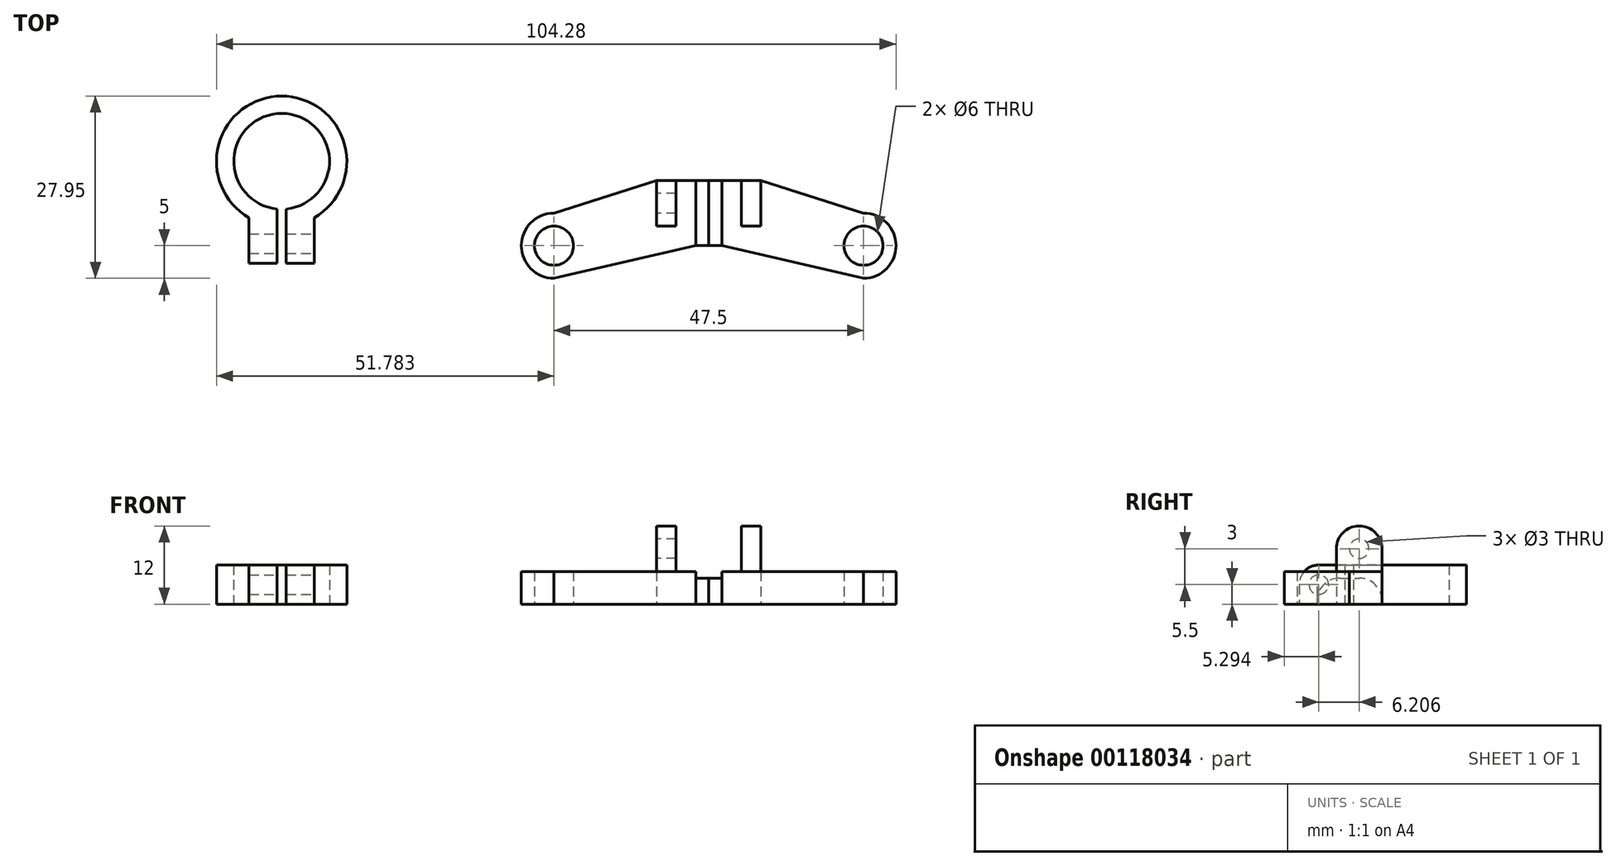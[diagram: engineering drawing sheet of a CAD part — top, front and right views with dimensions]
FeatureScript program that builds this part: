
annotation { "Feature Type Name" : "Feature", "Feature Type Description" : "" }
export const myFeature = defineFeature(function(context is Context, id is Id, definition is map)
    precondition{}
    {
        {
            var Q0;
            Q0=qCreatedBy(makeId("Top.planeOp"),FACE);
            var sketch = newSketch(context, id + "F0", { "sketchPlane" : qUnion([Q0])});
            skCircle(sketch, "E0", {"center": v(-31.45, 17.95) * mm, "radius": 7.35 * mm});
            skCircle(sketch, "E1", {"center": v(-31.45, 17.95) * mm, "radius": 10 * mm});
            skLineSegment(sketch, "E2", {"start": v(-26.45, 9.3) * mm, "end": v(-26.45, 2.3) * mm});
            skLineSegment(sketch, "E3", {"start": v(-26.45, 2.3) * mm, "end": v(-36.45, 2.3) * mm});
            skLineSegment(sketch, "E4", {"start": v(-36.45, 2.3) * mm, "end": v(-36.45, 9.3) * mm});
            skLineSegment(sketch, "E5", {"start": v(-32.15, 2.3) * mm, "end": v(-32.15, 10.64) * mm});
            skLineSegment(sketch, "E6", {"start": v(-30.75, 2.3) * mm, "end": v(-30.75, 10.64) * mm});
            skSolve(sketch);
        }
        {
            var Q0;
            {var subQ0=sQuery(id+"F0.wireOp",EDGE,"E2");Q0=makeQuery(id+"F0.imprint","IMPRINT",FACE,{"disambiguationData":[TD([[makeQuery(id+"F0.imprint","IMPRINT",EDGE,{"derivedFrom":subQ0}),-1.0]])]});}
            var Q1;
            {var subQ0=sQuery(id+"F0.wireOp",EDGE,"E4");Q1=makeQuery(id+"F0.imprint","IMPRINT",FACE,{"disambiguationData":[TD([[makeQuery(id+"F0.imprint","IMPRINT",EDGE,{"derivedFrom":subQ0}),-1.0]])]});}
            var Q2;
            {var subQ3=sQuery(id+"F0.wireOp",EDGE,"E5");var subQ4=sQuery(id+"F0.wireOp",EDGE,"E0");var subQ5=makeQuery(id+"F0.imprint","INTERSECT",VERTEX,{"derivedFrom":[subQ4,subQ3]});Q2=makeQuery(id+"F0.imprint","IMPRINT",FACE,{"disambiguationData":[TD([[makeQuery(id+"F0.imprint","IMPRINT",EDGE,{"disambiguationData":[TD([[subQ5,1.0]])],"derivedFrom":subQ4}),-1.0]])]});}
            extrude(context, id + "F1", {"entities" : qUnion([Q0, Q1, Q2]), "depth" : 6 * mm});
        }
        {
            var Q0;
            Q0=makeQuery(id+"F1.opExtrude","SWEPT_FACE",FACE,{"disambiguationData":[OSD([sQuery(id+"F0.wireOp",EDGE,"E2")])]});
            var sketch = newSketch(context, id + "F2", { "sketchPlane" : qUnion([Q0])});
            skPoint(sketch, "E7", {"position": v(5.3, 3) * mm});
            skSolve(sketch);
        }
        {
            var Q0;
            Q0=sQuery(id+"F2.wireOp",VERTEX,"E7");
            var Q1;
            Q1=makeQuery(id+"F1.opExtrude","SWEPT_BODY",BODY,{"disambiguationData":[OSD([sQuery(id+"F0.wireOp",EDGE,"E0"),sQuery(id+"F0.wireOp",EDGE,"E1"),sQuery(id+"F0.wireOp",EDGE,"E2"),sQuery(id+"F0.wireOp",EDGE,"E3"),sQuery(id+"F0.wireOp",EDGE,"E4")])]});
            hole(context, id + "F3", {"style" : HoleStyle.SIMPLE, "endStyle" : HoleEndStyle.THROUGH, "holeDiameter" : 3 * mm, "locations" : qUnion([Q0]), "scope" : qUnion([Q1]), "isTappedThrough" : true});
        }
        {
            var Q0;
            Q0=qCreatedBy(makeId("Top.planeOp"),FACE);
            var sketch = newSketch(context, id + "F4", { "sketchPlane" : qUnion([Q0])});
            skCircle(sketch, "E8", {"center": v(10.33, 5) * mm, "radius": 3 * mm});
            skLineSegment(sketch, "E9.left", {"start": v(5.33, 10) * mm, "end": v(5.33, 0) * mm});
            skPoint(sketch, "E10", {"position": v(10.33, 0) * mm});
            skPoint(sketch, "E11", {"position": v(34.08, 5) * mm});
            skLineSegment(sketch, "E12", {"start": v(34.08, 5) * mm, "end": v(32.08, 5) * mm});
            skLineSegment(sketch, "E13", {"start": v(32.08, 5) * mm, "end": v(10.33, 0) * mm});
            skPoint(sketch, "E14", {"position": v(29.08, 8) * mm});
            skPoint(sketch, "E15", {"position": v(26.08, 8) * mm});
            skLineSegment(sketch, "E16", {"start": v(26.08, 8) * mm, "end": v(26.08, 15) * mm});
            skLineSegment(sketch, "E17", {"start": v(34.08, 15) * mm, "end": v(26.08, 15) * mm});
            skLineSegment(sketch, "E18", {"start": v(29.08, 8) * mm, "end": v(29.08, 15) * mm});
            skPoint(sketch, "E19", {"position": v(32.08, 15) * mm});
            skLineSegment(sketch, "E20", {"start": v(32.08, 5) * mm, "end": v(32.08, 8) * mm});
            skPoint(sketch, "E21", {"position": v(10.33, 10) * mm});
            skPoint(sketch, "E22", {"position": v(26.08, 11.5) * mm});
            skLineSegment(sketch, "E23", {"start": v(32.08, 15) * mm, "end": v(32.08, 8) * mm});
            skLineSegment(sketch, "E24", {"start": v(5.33, 10) * mm, "end": v(10.33, 10) * mm});
            skLineSegment(sketch, "E25", {"start": v(5.33, 0) * mm, "end": v(10.33, 0) * mm});
            skLineSegment(sketch, "E26", {"start": v(26.08, 8) * mm, "end": v(29.08, 8) * mm});
            skLineSegment(sketch, "E27", {"start": v(29.08, 8) * mm, "end": v(32.08, 8) * mm});
            skLineSegment(sketch, "E28", {"start": v(34.08, 5) * mm, "end": v(34.08, 15) * mm});
            skLineSegment(sketch, "E29", {"start": v(10.33, 10) * mm, "end": v(26.08, 15) * mm});
            skSolve(sketch);
        }
        {
            var Q0;
            {var subQ0=sQuery(id+"F4.wireOp",EDGE,"E16");Q0=makeQuery(id+"F4.imprint","IMPRINT",FACE,{"disambiguationData":[TD([[makeQuery(id+"F4.imprint","IMPRINT",EDGE,{"derivedFrom":subQ0}),-1.0]])]});}
            extrude(context, id + "F5", {"entities" : qUnion([Q0]), "depth" : 12 * mm});
        }
        {
            var Q0;
            Q0=makeQuery(id+"F4.imprint","IMPRINT",FACE,{"disambiguationData":[TD([[makeQuery(id+"F4.imprint","IMPRINT",EDGE,{"derivedFrom":sQuery(id+"F4.wireOp",EDGE,"E8")}),-1.0]])]});
            var Q1;
            {var subQ0=sQuery(id+"F4.wireOp",EDGE,"E18");Q1=makeQuery(id+"F4.imprint","IMPRINT",FACE,{"disambiguationData":[TD([[makeQuery(id+"F4.imprint","IMPRINT",EDGE,{"derivedFrom":subQ0}),-1.0]])]});}
            var Q2;
            {var subQ3=sQuery(id+"F4.wireOp",EDGE,"1xFQyo0G-Xs1s-Fqlw-DN10-UjsStAcqlzeH");Q2=makeQuery(id+"F4.imprint","IMPRINT",FACE,{"disambiguationData":[TD([[makeQuery(id+"F4.imprint","IMPRINT",EDGE,{"derivedFrom":subQ3}),1.0]])]});}
            extrude(context, id + "F6", {"entities" : qUnion([Q0, Q1, Q2]), "operationType" : NewBodyOperationType.ADD, "depth" : 5 * mm});
        }
        {
            var Q0;
            {var subQ3=sQuery(id+"F4.wireOp",EDGE,"uUS1zDU1-sOwB-zFEP-Xbho-WG0gHNYcOc71");Q0=makeQuery(id+"F4.imprint","IMPRINT",FACE,{"disambiguationData":[TD([[makeQuery(id+"F4.imprint","IMPRINT",EDGE,{"derivedFrom":subQ3}),-1.0]])]});}
            var Q1;
            {var subQ4=sQuery(id+"F4.wireOp",EDGE,"E12");Q1=makeQuery(id+"F4.imprint","IMPRINT",FACE,{"disambiguationData":[TD([[makeQuery(id+"F4.imprint","IMPRINT",EDGE,{"derivedFrom":subQ4}),-1.0]])]});}
            var Q2;
            {var subQ1=sQuery(id+"F4.wireOp",EDGE,"N1TZ5UtL-Frhi-5IxH-qIdc-fXHmOs3rLAIg");Q2=makeQuery(id+"F4.imprint","IMPRINT",FACE,{"disambiguationData":[TD([[makeQuery(id+"F4.imprint","IMPRINT",EDGE,{"derivedFrom":subQ1}),1.0]])]});}
            extrude(context, id + "F7", {"entities" : qUnion([Q0, Q1, Q2]), "operationType" : NewBodyOperationType.ADD, "depth" : 4 * mm});
        }
        {
            var Q0;
            Q0=makeQuery(id+"F6.opExtrude","SWEPT_EDGE",EDGE,{"disambiguationData":[OSD([sQuery(id+"F4.wireOp",EDGE,"E9.top"),sQuery(id+"F4.wireOp",EDGE,"E9.left")])]});
            var Q1;
            Q1=makeQuery(id+"F6.opExtrude","SWEPT_EDGE",EDGE,{"disambiguationData":[OSD([sQuery(id+"F4.wireOp",EDGE,"E9.bottom"),sQuery(id+"F4.wireOp",EDGE,"E9.left")])]});
            fillet(context, id + "F8", {"entities" : qUnion([Q0, Q1]), "radius" : 5 * mm, "tangentPropagation" : true, "allowEdgeOverflow" : false});
        }
        {
            var Q0;
            {var subQ0=makeQuery(id+"F7.opExtrude","CAP_EDGE",EDGE,{"disambiguationData":[OSD([sQuery(id+"F4.wireOp",EDGE,"E17")])],"isStart":false});Q0=makeQuery(id+"F11.boolean.opBoolean","MERGE",EDGE,{"derivedFrom":[subQ0,makeQuery(id+"F11.opPattern","COPY",EDGE,{"derivedFrom":subQ0,"instanceName":"1"})]});}
            var Q1;
            {var subQ0=makeQuery(id+"F7.opExtrude","CAP_EDGE",EDGE,{"disambiguationData":[OSD([sQuery(id+"F4.wireOp",EDGE,"E12")])],"isStart":false});Q1=makeQuery(id+"F11.boolean.opBoolean","MERGE",EDGE,{"derivedFrom":[subQ0,makeQuery(id+"F11.opPattern","COPY",EDGE,{"derivedFrom":subQ0,"instanceName":"1"})]});}
            var Q2;
            Q2=makeQuery(id+"F5.opExtrude","CAP_EDGE",EDGE,{"disambiguationData":[OSD([sQuery(id+"F4.wireOp",EDGE,"E17")])],"isStart":false});
            var Q3;
            Q3=makeQuery(id+"F5.opExtrude","CAP_EDGE",EDGE,{"disambiguationData":[OSD([sQuery(id+"F4.wireOp",EDGE,"E9.bottom")])],"isStart":false});
            var Q4;
            Q4=makeQuery(id+"F5.opExtrude","CAP_EDGE",EDGE,{"disambiguationData":[OSD([sQuery(id+"F4.wireOp",EDGE,"E26")])],"isStart":false});
            fillet(context, id + "F9", {"entities" : qUnion([Q0, Q1, Q2, Q3, Q4]), "radius" : 3.5 * mm, "tangentPropagation" : true, "allowEdgeOverflow" : false});
        }
        {
            var Q0;
            Q0=makeQuery(id+"F5.opExtrude","SWEPT_FACE",FACE,{"disambiguationData":[OSD([sQuery(id+"F4.wireOp",EDGE,"E16")])]});
            var sketch = newSketch(context, id + "F10", { "sketchPlane" : qUnion([Q0])});
            skPoint(sketch, "E30", {"position": v(-11.5, 8.5) * mm});
            skSolve(sketch);
        }
        {
            var Q0;
            Q0=makeQuery(id+"F5.opExtrude","SWEPT_BODY",BODY,{"disambiguationData":[OSD([sQuery(id+"F4.wireOp",EDGE,"E9.bottom"),sQuery(id+"F4.wireOp",EDGE,"E16"),sQuery(id+"F4.wireOp",EDGE,"E17"),sQuery(id+"F4.wireOp",EDGE,"E18")])]});
            var Q1;
            Q1=makeQuery(id+"F7.opExtrude","SWEPT_FACE",FACE,{"disambiguationData":[OSD([sQuery(id+"F4.wireOp",EDGE,"E28")])]});
            mirror(context, id + "F11", {"operationType" : NewBodyOperationType.ADD, "entities" : qUnion([Q0]), "mirrorPlane" : qUnion([Q1])});
        }
        {
            var Q0;
            Q0=sQuery(id+"F10.wireOp",VERTEX,"E30");
            var Q1;
            Q1=makeQuery(id+"F5.opExtrude","SWEPT_BODY",BODY,{"disambiguationData":[OSD([sQuery(id+"F4.wireOp",EDGE,"E9.bottom"),sQuery(id+"F4.wireOp",EDGE,"E16"),sQuery(id+"F4.wireOp",EDGE,"E17"),sQuery(id+"F4.wireOp",EDGE,"E18")])]});
            hole(context, id + "F12", {"style" : HoleStyle.SIMPLE, "endStyle" : HoleEndStyle.THROUGH, "holeDiameter" : 3 * mm, "locations" : qUnion([Q0]), "scope" : qUnion([Q1]), "isTappedThrough" : true});
        }
        {
            var Q0;
            {var subQ0=sQuery(id+"F0.wireOp",EDGE,"E3");Q0=makeQuery(id+"F1.opExtrude","CAP_EDGE",EDGE,{"disambiguationData":[OSD([subQ0]),TDD([makeQuery(id+"F0.imprint","IMPRINT",EDGE,{"disambiguationData":[TD([[makeQuery(id+"F0.imprint","INTERSECT",VERTEX,{"derivedFrom":[subQ0,sQuery(id+"F0.wireOp",EDGE,"E4")]}),1.0]])],"derivedFrom":subQ0})])],"isStart":false});}
            var Q1;
            {var subQ0=sQuery(id+"F0.wireOp",EDGE,"E3");Q1=makeQuery(id+"F1.opExtrude","CAP_EDGE",EDGE,{"disambiguationData":[OSD([subQ0]),TDD([makeQuery(id+"F0.imprint","IMPRINT",EDGE,{"disambiguationData":[TD([[makeQuery(id+"F0.imprint","INTERSECT",VERTEX,{"derivedFrom":[sQuery(id+"F0.wireOp",EDGE,"E2"),subQ0]}),-1.0]])],"derivedFrom":subQ0})])],"isStart":false});}
            fillet(context, id + "F13", {"entities" : qUnion([Q0, Q1]), "radius" : 3 * mm, "tangentPropagation" : true, "allowEdgeOverflow" : false});
        }
    });
